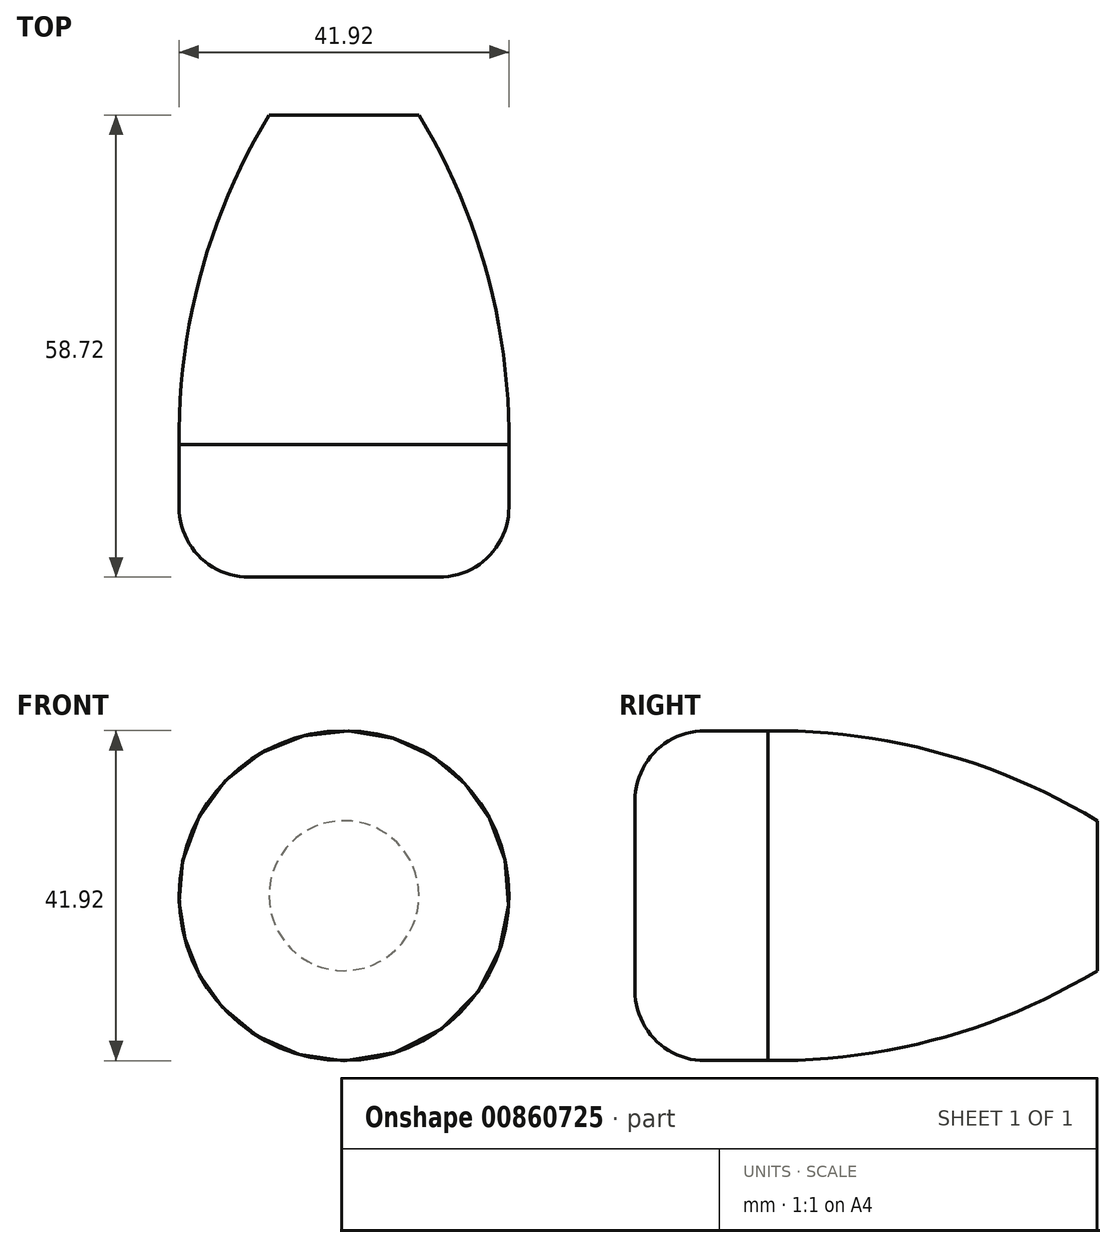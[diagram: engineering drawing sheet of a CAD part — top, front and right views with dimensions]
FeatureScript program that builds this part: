
annotation { "Feature Type Name" : "Feature", "Feature Type Description" : "" }
export const myFeature = defineFeature(function(context is Context, id is Id, definition is map)
    precondition{}
    {
        {
            var Q0;
            Q0=qCreatedBy(makeId("Right.planeOp"),FACE);
            var sketch = newSketch(context, id + "F0", { "sketchPlane" : qUnion([Q0])});
            skLineSegment(sketch, "E0", {"start": v(0, 0) * mm, "end": v(0, 12.06) * mm});
            skArc(sketch, "E1", {"start": v(58.72, 9.52) * mm, "mid": v(38.6, 18.16) * mm, "end": v(16.86, 20.95) * mm});
            skLineSegment(sketch, "E2", {"start": v(58.72, 9.52) * mm, "end": v(58.72, 0) * mm});
            skLineSegment(sketch, "E3", {"start": v(0, 0) * mm, "end": v(58.72, 0) * mm});
            skLineSegment(sketch, "E4", {"start": v(16.86, 20.95) * mm, "end": v(8.9, 20.95) * mm});
            skPoint(sketch, "E5.visualSharp", {"position": v(0, 20.95) * mm});
            skArc(sketch, "E5.filletArc", {"start": v(8.9, 20.95) * mm, "mid": v(2.6, 18.35) * mm, "end": v(0, 12.06) * mm});
            skSolve(sketch);
        }
        {
            var Q0;
            Q0=qSketchRegion(id+"F0",true);
            var Q1;
            Q1=sQuery(id+"F0.wireOp",EDGE,"E3");
            revolve(context, id + "F1", {"entities" : qUnion([Q0]), "axis" : qUnion([Q1]), "revolveType" : RevolveType.FULL});
        }
    });
